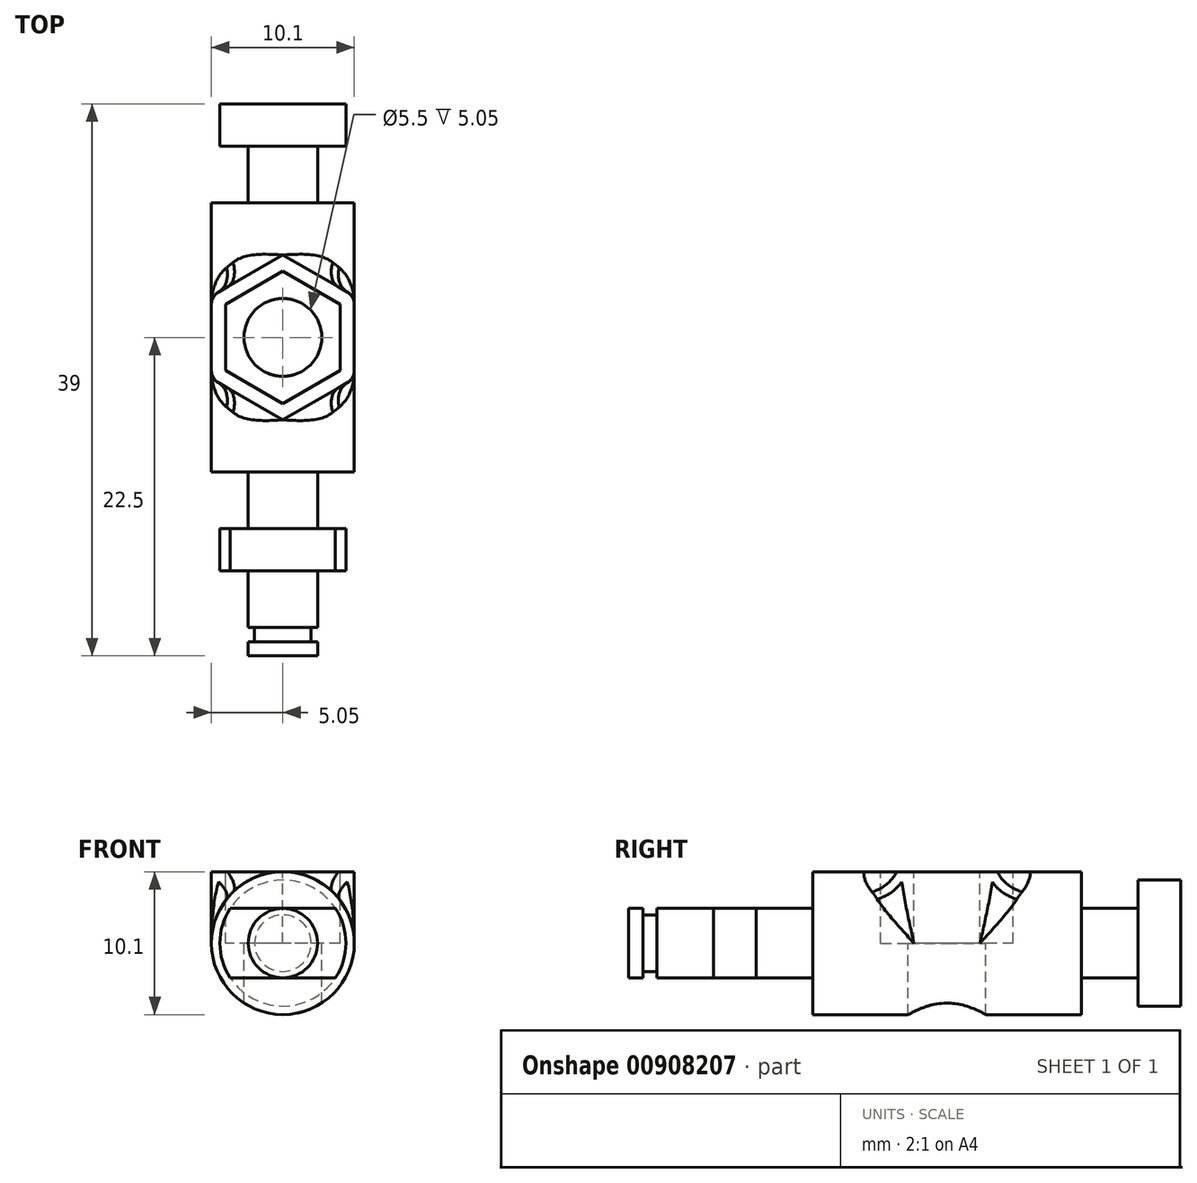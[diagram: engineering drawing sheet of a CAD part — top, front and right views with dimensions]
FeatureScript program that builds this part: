
annotation { "Feature Type Name" : "Feature", "Feature Type Description" : "" }
export const myFeature = defineFeature(function(context is Context, id is Id, definition is map)
    precondition{}
    {
        {
            var Q0;
            Q0=qCreatedBy(makeId("Top.planeOp"),FACE);
            var sketch = newSketch(context, id + "F0", { "sketchPlane" : qUnion([Q0])});
            skLineSegment(sketch, "E0", {"start": v(0, 16.5) * mm, "end": v(-4.45, 16.5) * mm});
            skLineSegment(sketch, "E1", {"start": v(-4.45, 16.5) * mm, "end": v(-4.45, 13.5) * mm});
            skLineSegment(sketch, "E2", {"start": v(-4.45, 13.5) * mm, "end": v(-2.45, 13.5) * mm});
            skLineSegment(sketch, "E3", {"start": v(-2.45, 13.5) * mm, "end": v(-2.45, 9.5) * mm});
            skLineSegment(sketch, "E4", {"start": v(-2.45, 9.5) * mm, "end": v(-5.05, 9.5) * mm});
            skLineSegment(sketch, "E5", {"start": v(-5.05, 9.5) * mm, "end": v(-5.05, 0) * mm});
            skLineSegment(sketch, "E6", {"start": v(0, 0) * mm, "end": v(37.33, 0) * mm, "construction": true});
            skLineSegment(sketch, "E7", {"start": v(0, 0) * mm, "end": v(0, 29.63) * mm, "construction": true});
            skLineSegment(sketch, "E8.MirrorCS", {"start": v(-5.05, -9.5) * mm, "end": v(-5.05, 0) * mm});
            skLineSegment(sketch, "E9.MirrorCS", {"start": v(-2.45, -9.5) * mm, "end": v(-5.05, -9.5) * mm});
            skLineSegment(sketch, "E10.MirrorCS", {"start": v(-2.45, -13.5) * mm, "end": v(-2.45, -9.5) * mm});
            skLineSegment(sketch, "E11.MirrorCS", {"start": v(-4.45, -13.5) * mm, "end": v(-2.45, -13.5) * mm});
            skLineSegment(sketch, "E12.MirrorCS", {"start": v(-4.45, -16.5) * mm, "end": v(-4.45, -13.5) * mm});
            skLineSegment(sketch, "E13.MirrorCS", {"start": v(0, -16.5) * mm, "end": v(-4.45, -16.5) * mm});
            skLineSegment(sketch, "E14", {"start": v(0, 16.5) * mm, "end": v(0, -16.5) * mm});
            skSolve(sketch);
        }
        {
            var Q0;
            Q0 = qSketchRegion(id + "F0", true);
            var Q1;
            Q1=sQuery(id+"F0.wireOp",EDGE,"E7");
            revolve(context, id + "F1", {"surfaceOperationType" : NewSurfaceOperationType.NEW, "entities" : qUnion([Q0]), "axis" : qUnion([Q1]), "revolveType" : RevolveType.FULL});
        }
        {
            var Q0;
            Q0=qCreatedBy(makeId("Top.planeOp"),FACE);
            cPlane(context, id + "F2", {"entities" : qUnion([Q0]), "cplaneType" : CPlaneType.OFFSET, "offset" : 10 * mm, "width" : 150 * mm, "height" : 150 * mm});
        }
        {
            var Q0;
            Q0=qCreatedBy(makeId("Top.planeOp"),FACE);
            var sketch = newSketch(context, id + "F3", { "sketchPlane" : qUnion([Q0])});
            skLineSegment(sketch, "E15.bottom", {"start": v(0, -9.5) * mm, "end": v(-20, -9.5) * mm});
            skLineSegment(sketch, "E15.top", {"start": v(0, 9.5) * mm, "end": v(-20, 9.5) * mm});
            skLineSegment(sketch, "E15.left", {"start": v(0, -9.5) * mm, "end": v(0, 9.5) * mm});
            skLineSegment(sketch, "E15.right", {"start": v(-20, -9.5) * mm, "end": v(-20, 9.5) * mm});
            skSolve(sketch);
        }
        {
            var Q0;
            Q0=qCreatedBy(id+"F2.planeOp",FACE);
            var sketch = newSketch(context, id + "F4", { "sketchPlane" : qUnion([Q0])});
            skCircle(sketch, "E16.cCircle", {"center": v(0, 0) * mm, "radius": 4.05 * mm, "construction": true});
            skLineSegment(sketch, "E16.0", {"start": v(0, -4.68) * mm, "end": v(-4.05, -2.34) * mm});
            skLineSegment(sketch, "E16.1", {"start": v(-4.05, -2.34) * mm, "end": v(-4.05, 2.34) * mm});
            skLineSegment(sketch, "E16.2", {"start": v(-4.05, 2.34) * mm, "end": v(0, 4.68) * mm});
            skLineSegment(sketch, "E16.3", {"start": v(0, 4.68) * mm, "end": v(4.05, 2.34) * mm});
            skLineSegment(sketch, "E16.4", {"start": v(4.05, 2.34) * mm, "end": v(4.05, -2.34) * mm});
            skLineSegment(sketch, "E16.5", {"start": v(4.05, -2.34) * mm, "end": v(0, -4.68) * mm});
            skPoint(sketch, "E16.0.midPoint", {"position": v(-2.03, -3.5) * mm});
            skSolve(sketch);
        }
        {
            var Q0;
            Q0=makeQuery(id+"F4.imprint","IMPRINT",FACE,{"disambiguationData":[TD([[makeQuery(id+"F4.imprint","IMPRINT",EDGE,{"derivedFrom":sQuery(id+"F4.wireOp",EDGE,"E16.0")}),-1.0]])]});
            extrude(context, id + "F5", {"entities" : qUnion([Q0]), "operationType" : NewBodyOperationType.REMOVE, "oppositeDirection" : true, "depth" : 10 * mm, "offsetDistance" : 25 * mm});
        }
        {
            var Q0;
            Q0=makeQuery(id+"F5.boolean.opBoolean","COPY",FACE,{"derivedFrom":makeQuery(id+"F5.opExtrude","CAP_FACE",FACE,{"disambiguationData":[OSD([sQuery(id+"F4.wireOp",EDGE,"E16.0"),sQuery(id+"F4.wireOp",EDGE,"E16.1"),sQuery(id+"F4.wireOp",EDGE,"E16.2"),sQuery(id+"F4.wireOp",EDGE,"E16.3"),sQuery(id+"F4.wireOp",EDGE,"E16.4"),sQuery(id+"F4.wireOp",EDGE,"E16.5")])],"isStart":false})});
            var sketch = newSketch(context, id + "F6", { "sketchPlane" : qUnion([Q0])});
            skCircle(sketch, "E17", {"center": v(0, 0) * mm, "radius": 2.75 * mm});
            skSolve(sketch);
        }
        {
            var Q0;
            Q0 = qSketchRegion(id + "F6", true);
            extrude(context, id + "F7", {"entities" : qUnion([Q0]), "operationType" : NewBodyOperationType.REMOVE, "endBound" : BoundingType.UP_TO_NEXT, "oppositeDirection" : true, "depth" : 25 * mm, "offsetDistance" : 25 * mm});
        }
        {
            var Q0;
            Q0=makeQuery(id+"F5.boolean.opBoolean","COPY",FACE,{"derivedFrom":makeQuery(id+"F5.opExtrude","CAP_FACE",FACE,{"disambiguationData":[OSD([sQuery(id+"F4.wireOp",EDGE,"E16.0"),sQuery(id+"F4.wireOp",EDGE,"E16.1"),sQuery(id+"F4.wireOp",EDGE,"E16.2"),sQuery(id+"F4.wireOp",EDGE,"E16.3"),sQuery(id+"F4.wireOp",EDGE,"E16.4"),sQuery(id+"F4.wireOp",EDGE,"E16.5")])],"isStart":false})});
            var sketch = newSketch(context, id + "F8", { "sketchPlane" : qUnion([Q0])});
            skSolve(sketch);
        }
        {
            var Q0;
            Q0=makeQuery(id+"F8.imprint","IMPRINT",FACE,{"disambiguationData":[TD([[makeQuery(id+"F8.imprint","IMPRINT",EDGE,{"derivedFrom":makeQuery(id+"F5.boolean.opBoolean","COPY",EDGE,{"derivedFrom":makeQuery(id+"F5.opExtrude","CAP_EDGE",EDGE,{"disambiguationData":[OSD([sQuery(id+"F4.wireOp",EDGE,"E16.0")])],"isStart":false})})}),-1.0]])]});
            var sketch = newSketch(context, id + "F9", { "sketchPlane" : qUnion([Q0])});
            skLineSegment(sketch, "E18.0.0", {"start": v(0, -4.68) * mm, "end": v(4.05, -2.34) * mm});
            skLineSegment(sketch, "E18.0.1", {"start": v(4.05, -2.34) * mm, "end": v(4.05, 2.34) * mm});
            skLineSegment(sketch, "E18.0.2", {"start": v(4.05, 2.34) * mm, "end": v(0, 4.68) * mm});
            skLineSegment(sketch, "E18.0.3", {"start": v(0, 4.68) * mm, "end": v(-4.05, 2.34) * mm});
            skLineSegment(sketch, "E18.0.4", {"start": v(-4.05, 2.34) * mm, "end": v(-4.05, -2.34) * mm});
            skLineSegment(sketch, "E18.0.5", {"start": v(-4.05, -2.34) * mm, "end": v(0, -4.68) * mm});
            skLineSegment(sketch, "E19.0", {"start": v(-5.05, -2.92) * mm, "end": v(0, -5.83) * mm});
            skLineSegment(sketch, "E19.1", {"start": v(5.05, -2.92) * mm, "end": v(5.05, 2.92) * mm});
            skLineSegment(sketch, "E19.2", {"start": v(5.05, 2.92) * mm, "end": v(0, 5.83) * mm});
            skLineSegment(sketch, "E19.3", {"start": v(0, -5.83) * mm, "end": v(5.05, -2.92) * mm});
            skLineSegment(sketch, "E19.4", {"start": v(0, 5.83) * mm, "end": v(-5.05, 2.92) * mm});
            skLineSegment(sketch, "E19.5", {"start": v(-5.05, 2.92) * mm, "end": v(-5.05, -2.92) * mm});
            skSolve(sketch);
        }
        {
            var Q0;
            Q0 = qSketchRegion(id + "F9", true);
            var Q1;
            Q1=makeQuery(id+"F5.boolean.opBoolean","INTERSECT",VERTEX,{"derivedFrom":[makeQuery(id+"F1.opRevolve","SWEPT_FACE",FACE,{"disambiguationData":[OSD([sQuery(id+"F0.wireOp",EDGE,"E5"),sQuery(id+"F0.wireOp",EDGE,"E8.MirrorCS")])]}),makeQuery(id+"F5.opExtrude","SWEPT_FACE",FACE,{"disambiguationData":[OSD([sQuery(id+"F4.wireOp",EDGE,"E16.2")])]}),makeQuery(id+"F5.opExtrude","SWEPT_FACE",FACE,{"disambiguationData":[OSD([sQuery(id+"F4.wireOp",EDGE,"E16.3")])]})]});
            extrude(context, id + "F10", {"entities" : qUnion([Q0]), "operationType" : NewBodyOperationType.ADD, "endBound" : BoundingType.UP_TO_VERTEX, "depth" : 25 * mm, "endBoundEntityVertex" : qUnion([Q1]), "offsetDistance" : 25 * mm});
        }
        {
            var Q0;
            Q0=makeQuery(id+"F10.opExtrude","SWEPT_EDGE",EDGE,{"disambiguationData":[OSD([sQuery(id+"F9.wireOp",EDGE,"E19.0"),sQuery(id+"F9.wireOp",EDGE,"E19.5")])]});
            var Q1;
            Q1=makeQuery(id+"F10.opExtrude","SWEPT_EDGE",EDGE,{"disambiguationData":[OSD([sQuery(id+"F9.wireOp",EDGE,"E19.4"),sQuery(id+"F9.wireOp",EDGE,"E19.5")])]});
            var Q2;
            Q2=makeQuery(id+"F10.opExtrude","SWEPT_EDGE",EDGE,{"disambiguationData":[OSD([sQuery(id+"F9.wireOp",EDGE,"E19.1"),sQuery(id+"F9.wireOp",EDGE,"E19.3")])]});
            var Q3;
            Q3=makeQuery(id+"F10.opExtrude","SWEPT_EDGE",EDGE,{"disambiguationData":[OSD([sQuery(id+"F9.wireOp",EDGE,"E19.1"),sQuery(id+"F9.wireOp",EDGE,"E19.2")])]});
            fillet(context, id + "F11", {"entities" : qUnion([Q0, Q1, Q2, Q3]), "tangentPropagation" : true, "radius" : 1 * mm, "defaultsChanged" : false, "vertexSettings" : [], "allowEdgeOverflow" : false});
        }
        {
            var Q0;
            Q0=makeQuery(id+"F10.boolean.opBoolean","INTERSECT",EDGE,{"derivedFrom":[makeQuery(id+"F1.opRevolve","SWEPT_FACE",FACE,{"disambiguationData":[OSD([sQuery(id+"F0.wireOp",EDGE,"E5"),sQuery(id+"F0.wireOp",EDGE,"E8.MirrorCS")])]}),makeQuery(id+"F10.opExtrude","SWEPT_FACE",FACE,{"disambiguationData":[OSD([sQuery(id+"F9.wireOp",EDGE,"E19.3")])]})]});
            var Q1;
            Q1=makeQuery(id+"F10.boolean.opBoolean","INTERSECT",EDGE,{"derivedFrom":[makeQuery(id+"F1.opRevolve","SWEPT_FACE",FACE,{"disambiguationData":[OSD([sQuery(id+"F0.wireOp",EDGE,"E5"),sQuery(id+"F0.wireOp",EDGE,"E8.MirrorCS")])]}),makeQuery(id+"F10.opExtrude","SWEPT_FACE",FACE,{"disambiguationData":[OSD([sQuery(id+"F9.wireOp",EDGE,"E19.0")])]})]});
            var Q2;
            Q2=makeQuery(id+"F10.boolean.opBoolean","INTERSECT",EDGE,{"derivedFrom":[makeQuery(id+"F1.opRevolve","SWEPT_FACE",FACE,{"disambiguationData":[OSD([sQuery(id+"F0.wireOp",EDGE,"E5"),sQuery(id+"F0.wireOp",EDGE,"E8.MirrorCS")])]}),makeQuery(id+"F10.opExtrude","SWEPT_FACE",FACE,{"disambiguationData":[OSD([sQuery(id+"F9.wireOp",EDGE,"E19.2")])]})]});
            var Q3;
            Q3=makeQuery(id+"F10.boolean.opBoolean","INTERSECT",EDGE,{"derivedFrom":[makeQuery(id+"F1.opRevolve","SWEPT_FACE",FACE,{"disambiguationData":[OSD([sQuery(id+"F0.wireOp",EDGE,"E5"),sQuery(id+"F0.wireOp",EDGE,"E8.MirrorCS")])]}),makeQuery(id+"F10.opExtrude","SWEPT_FACE",FACE,{"disambiguationData":[OSD([sQuery(id+"F9.wireOp",EDGE,"E19.4")])]})]});
            fillet(context, id + "F12", {"entities" : qUnion([Q0, Q1, Q2, Q3]), "tangentPropagation" : true, "radius" : 2 * mm, "defaultsChanged" : true, "vertexSettings" : [], "allowEdgeOverflow" : false});
        }
        {
            var Q0;
            Q0=makeQuery(id+"F1.opRevolve","SWEPT_FACE",FACE,{"disambiguationData":[OSD([sQuery(id+"F0.wireOp",EDGE,"E13.MirrorCS")])]});
            var sketch = newSketch(context, id + "F13", { "sketchPlane" : qUnion([Q0])});
            skLineSegment(sketch, "E20.bottom", {"start": v(-4.45, -4.45) * mm, "end": v(4.45, -4.45) * mm});
            skLineSegment(sketch, "E20.top", {"start": v(-4.45, -2.45) * mm, "end": v(4.45, -2.45) * mm});
            skLineSegment(sketch, "E20.left", {"start": v(-4.45, -4.45) * mm, "end": v(-4.45, -2.45) * mm});
            skLineSegment(sketch, "E20.right", {"start": v(4.45, -4.45) * mm, "end": v(4.45, -2.45) * mm});
            skLineSegment(sketch, "E21", {"start": v(0, 0) * mm, "end": v(-14.7, 0) * mm, "construction": true});
            skLineSegment(sketch, "E22.MirrorCS", {"start": v(-4.45, 2.45) * mm, "end": v(4.45, 2.45) * mm});
            skLineSegment(sketch, "E23.MirrorCS", {"start": v(-4.45, 4.45) * mm, "end": v(-4.45, 2.45) * mm});
            skLineSegment(sketch, "E24.MirrorCS", {"start": v(-4.45, 4.45) * mm, "end": v(4.45, 4.45) * mm});
            skLineSegment(sketch, "E25.MirrorCS", {"start": v(4.45, 4.45) * mm, "end": v(4.45, 2.45) * mm});
            skSolve(sketch);
        }
        {
            var Q0;
            Q0 = qSketchRegion(id + "F13", true);
            var Q1;
            Q1=makeQuery(id+"F1.opRevolve","SWEPT_FACE",FACE,{"disambiguationData":[OSD([sQuery(id+"F0.wireOp",EDGE,"E9.MirrorCS")])]});
            extrude(context, id + "F14", {"entities" : qUnion([Q0]), "operationType" : NewBodyOperationType.REMOVE, "oppositeDirection" : true, "depth" : 4 * mm, "endBoundEntityFace" : qUnion([Q1]), "offsetDistance" : 25 * mm});
        }
        {
            var Q0;
            Q0=makeQuery(id+"F1.opRevolve","SWEPT_FACE",FACE,{"disambiguationData":[OSD([sQuery(id+"F0.wireOp",EDGE,"E13.MirrorCS")])]});
            var sketch = newSketch(context, id + "F15", { "sketchPlane" : qUnion([Q0])});
            skCircle(sketch, "E26", {"center": v(0, 0) * mm, "radius": 2.45 * mm});
            skSolve(sketch);
        }
        {
            var Q0;
            Q0 = qSketchRegion(id + "F15", true);
            extrude(context, id + "F16", {"entities" : qUnion([Q0]), "operationType" : NewBodyOperationType.ADD, "depth" : 6 * mm, "offsetDistance" : 25 * mm});
        }
        {
            var Q0;
            Q0=makeQuery(id+"F16.opExtrude","CAP_FACE",FACE,{"disambiguationData":[OSD([sQuery(id+"F15.wireOp",EDGE,"E26")])],"isStart":false});
            var sketch = newSketch(context, id + "F17", { "sketchPlane" : qUnion([Q0])});
            skCircle(sketch, "E27", {"center": v(0, 0) * mm, "radius": 1.25 * mm});
            skSolve(sketch);
        }
        {
            var Q0;
            Q0=makeQuery(id+"F17.imprint","IMPRINT",FACE,{"disambiguationData":[TD([[makeQuery(id+"F17.imprint","IMPRINT",EDGE,{"derivedFrom":sQuery(id+"F17.wireOp",EDGE,"E27")}),-1.0]])]});
            cPlane(context, id + "F18", {"entities" : qUnion([Q0]), "cplaneType" : CPlaneType.OFFSET, "offset" : 1 * mm, "oppositeDirection" : true, "width" : 150 * mm, "height" : 150 * mm});
        }
        {
            var Q0;
            Q0=qCreatedBy(id+"F18.planeOp",FACE);
            var sketch = newSketch(context, id + "F19", { "sketchPlane" : qUnion([Q0])});
            skCircle(sketch, "E28", {"center": v(0, 0) * mm, "radius": 2 * mm});
            skCircle(sketch, "E29", {"center": v(0, 0) * mm, "radius": 2.8 * mm});
            skSolve(sketch);
        }
        {
            var Q0;
            Q0 = qSketchRegion(id + "F19", true);
            extrude(context, id + "F20", {"entities" : qUnion([Q0]), "operationType" : NewBodyOperationType.REMOVE, "oppositeDirection" : true, "depth" : 1 * mm, "offsetDistance" : 25 * mm});
        }
    });
